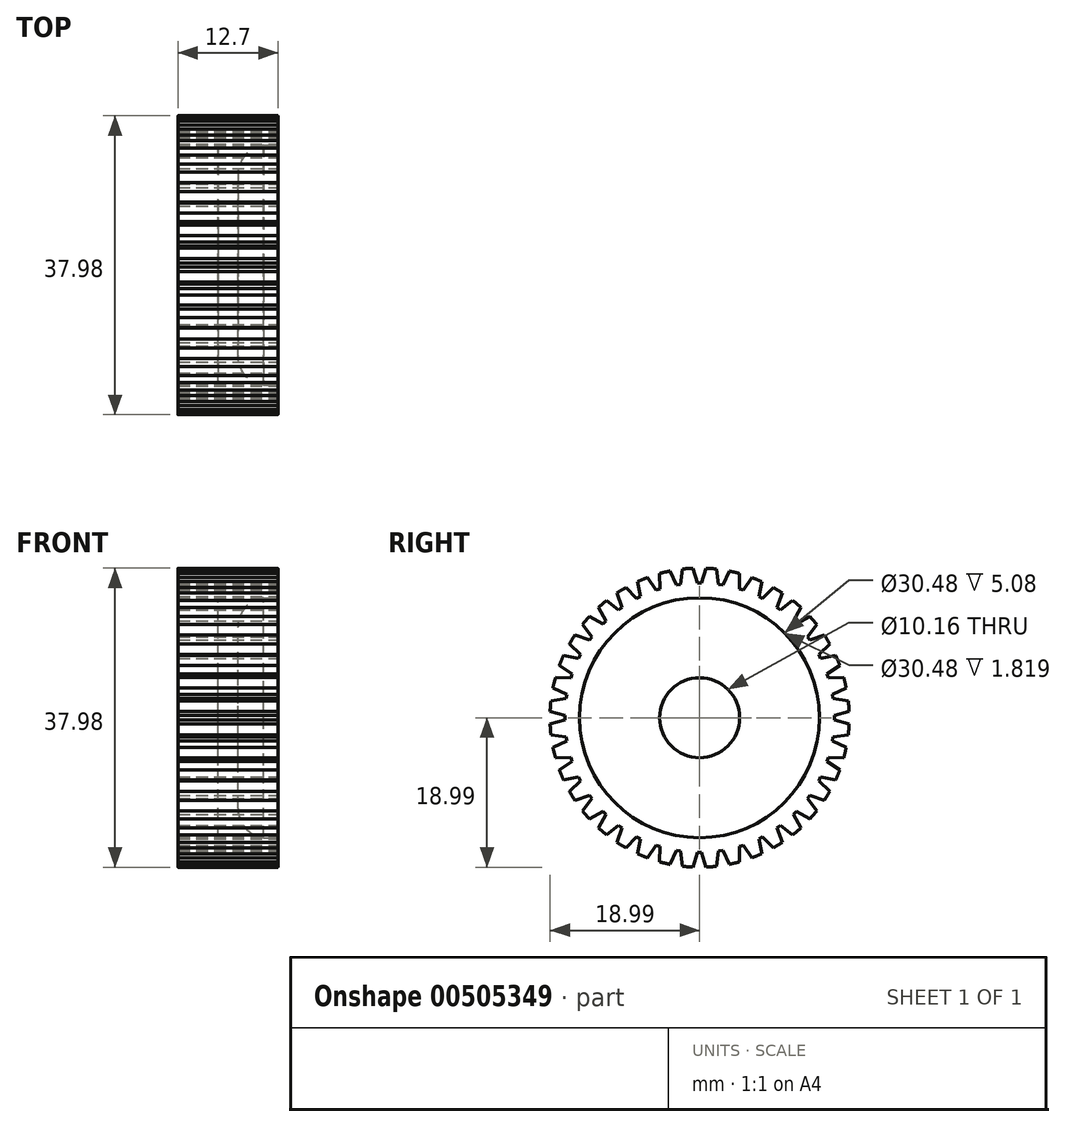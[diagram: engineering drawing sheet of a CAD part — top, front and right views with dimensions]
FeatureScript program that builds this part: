
annotation { "Feature Type Name" : "Feature", "Feature Type Description" : "" }
export const myFeature = defineFeature(function(context is Context, id is Id, definition is map)
    precondition{}
    {
        {
            var Q0;
            Q0=qCreatedBy(makeId("Top.planeOp"),FACE);
            var sketch = newSketch(context, id + "F0", { "sketchPlane" : qUnion([Q0])});
            skLineSegment(sketch, "E0", {"start": v(0, 0) * mm, "end": v(-12.7, 0) * mm, "construction": true});
            skLineSegment(sketch, "E1", {"start": v(0, 0) * mm, "end": v(0, 50.8) * mm, "construction": true});
            skLineSegment(sketch, "E2", {"start": v(0, 5.08) * mm, "end": v(0, 15.24) * mm});
            skLineSegment(sketch, "E3", {"start": v(0, 15.24) * mm, "end": v(5.08, 15.24) * mm});
            skArc(sketch, "E4", {"start": v(3.26, 15.24) * mm, "mid": v(0.93, 14) * mm, "end": v(0, 11.54) * mm});
            skLineSegment(sketch, "E5.bottom", {"start": v(0, 5.08) * mm, "end": v(-2.54, 5.08) * mm});
            skLineSegment(sketch, "E5.top", {"start": v(0, 15.24) * mm, "end": v(-2.54, 15.24) * mm});
            skLineSegment(sketch, "E5.right", {"start": v(-2.54, 5.08) * mm, "end": v(-2.54, 15.24) * mm});
            skLineSegment(sketch, "E6", {"start": v(-1.27, 15.24) * mm, "end": v(-1.27, 4.9) * mm, "construction": true});
            skPoint(sketch, "E6.endSnap0", {"position": v(-1.27, 5.08) * mm});
            skArc(sketch, "E7.MirrorCS", {"start": v(-5.8, 15.24) * mm, "mid": v(-3.47, 14) * mm, "end": v(-2.54, 11.54) * mm});
            skLineSegment(sketch, "E8.MirrorCS", {"start": v(-2.54, 15.24) * mm, "end": v(-7.62, 15.24) * mm});
            skLineSegment(sketch, "E9.bottom", {"start": v(-7.62, 15.24) * mm, "end": v(5.08, 15.24) * mm});
            skLineSegment(sketch, "E9.top", {"start": v(-7.62, 19) * mm, "end": v(5.08, 19) * mm});
            skLineSegment(sketch, "E9.left", {"start": v(-7.62, 15.24) * mm, "end": v(-7.62, 19) * mm});
            skLineSegment(sketch, "E9.right", {"start": v(5.08, 15.24) * mm, "end": v(5.08, 19) * mm});
            skSolve(sketch);
        }
        {
            var Q0;
            Q0=makeQuery(id+"F0.imprint","IMPRINT",FACE,{"disambiguationData":[TD([[makeQuery(id+"F0.imprint","IMPRINT",EDGE,{"derivedFrom":sQuery(id+"F0.wireOp",EDGE,"E9.top")}),-1.0]])]});
            var Q1;
            {var subQ3=sQuery(id+"F0.wireOp",EDGE,"E7.MirrorCS");Q1=makeQuery(id+"F0.imprint","IMPRINT",FACE,{"disambiguationData":[TD([[makeQuery(id+"F0.imprint","IMPRINT",EDGE,{"derivedFrom":subQ3}),1.0]])]});}
            var Q2;
            {var subQ1=sQuery(id+"F0.wireOp",EDGE,"E5.bottom");Q2=makeQuery(id+"F0.imprint","IMPRINT",FACE,{"disambiguationData":[TD([[makeQuery(id+"F0.imprint","IMPRINT",EDGE,{"derivedFrom":subQ1}),-1.0]])]});}
            var Q3;
            {var subQ0=sQuery(id+"F0.wireOp",EDGE,"E4");Q3=makeQuery(id+"F0.imprint","IMPRINT",FACE,{"disambiguationData":[TD([[makeQuery(id+"F0.imprint","IMPRINT",EDGE,{"derivedFrom":subQ0}),-1.0]])]});}
            var Q4;
            Q4=sQuery(id+"F0.wireOp",EDGE,"E0");
            revolve(context, id + "F1", {"entities" : qUnion([Q0, Q1, Q2, Q3]), "axis" : qUnion([Q4]), "revolveType" : RevolveType.FULL});
        }
        {
            var Q0;
            Q0=makeQuery(id+"F1.opRevolve","SWEPT_FACE",FACE,{"disambiguationData":[OSD([sQuery(id+"F0.wireOp",EDGE,"E9.right")])]});
            var sketch = newSketch(context, id + "F2", { "sketchPlane" : qUnion([Q0])});
            skLineSegment(sketch, "E10", {"start": v(0, 19) * mm, "end": v(0, 15.24) * mm, "construction": true});
            skLineSegment(sketch, "E11", {"start": v(0, 19) * mm, "end": v(0, 17.12) * mm});
            skLineSegment(sketch, "E12", {"start": v(0, 17.12) * mm, "end": v(0.26, 17.12) * mm});
            skLineSegment(sketch, "E13", {"start": v(0.26, 17.12) * mm, "end": v(0.82, 18.99) * mm});
            skLineSegment(sketch, "E14.MirrorCS", {"start": v(-0.26, 17.12) * mm, "end": v(-0.82, 18.99) * mm});
            skLineSegment(sketch, "E15.MirrorCS", {"start": v(0, 17.12) * mm, "end": v(-0.26, 17.12) * mm});
            skSolve(sketch);
        }
        {
            var Q0;
            {var subQ0=sQuery(id+"F2.wireOp",EDGE,"E11");Q0=makeQuery(id+"F2.imprint","IMPRINT",FACE,{"disambiguationData":[TD([[makeQuery(id+"F2.imprint","IMPRINT",EDGE,{"derivedFrom":subQ0}),-1.0]])]});}
            var Q1;
            {var subQ0=sQuery(id+"F2.wireOp",EDGE,"E11");Q1=makeQuery(id+"F2.imprint","IMPRINT",FACE,{"disambiguationData":[TD([[makeQuery(id+"F2.imprint","IMPRINT",EDGE,{"derivedFrom":subQ0}),1.0]])]});}
            extrude(context, id + "F3", {"entities" : qUnion([Q0, Q1]), "operationType" : NewBodyOperationType.REMOVE, "oppositeDirection" : true, "depth" : 25.4 * mm});
        }
        {
            var Q0;
            Q0=makeQuery(id+"F3.boolean.opBoolean","COPY",FACE,{"derivedFrom":makeQuery(id+"F3.opExtrude","SWEPT_FACE",FACE,{"disambiguationData":[OSD([sQuery(id+"F2.wireOp",EDGE,"E13")])]})});
            var Q1;
            Q1=makeQuery(id+"F3.boolean.opBoolean","COPY",FACE,{"derivedFrom":makeQuery(id+"F3.opExtrude","SWEPT_FACE",FACE,{"disambiguationData":[OSD([sQuery(id+"F2.wireOp",EDGE,"E12"),sQuery(id+"F2.wireOp",EDGE,"E15.MirrorCS")])]})});
            var Q2;
            Q2=makeQuery(id+"F3.boolean.opBoolean","COPY",FACE,{"derivedFrom":makeQuery(id+"F3.opExtrude","SWEPT_FACE",FACE,{"disambiguationData":[OSD([sQuery(id+"F2.wireOp",EDGE,"E14.MirrorCS")])]})});
            var Q3;
            Q3=makeQuery(id+"F1.opRevolve","SWEPT_EDGE",EDGE,{"disambiguationData":[OSD([sQuery(id+"F0.wireOp",EDGE,"E5.bottom"),sQuery(id+"F0.wireOp",EDGE,"E2")])]});
            circularPattern(context, id + "F4", {"patternType" : PatternType.FACE, "faces" : qUnion([Q0, Q1, Q2]), "axis" : qUnion([Q3]), "angle" : 360 * degree, "instanceCount" : 40, "equalSpace" : true});
        }
    });
